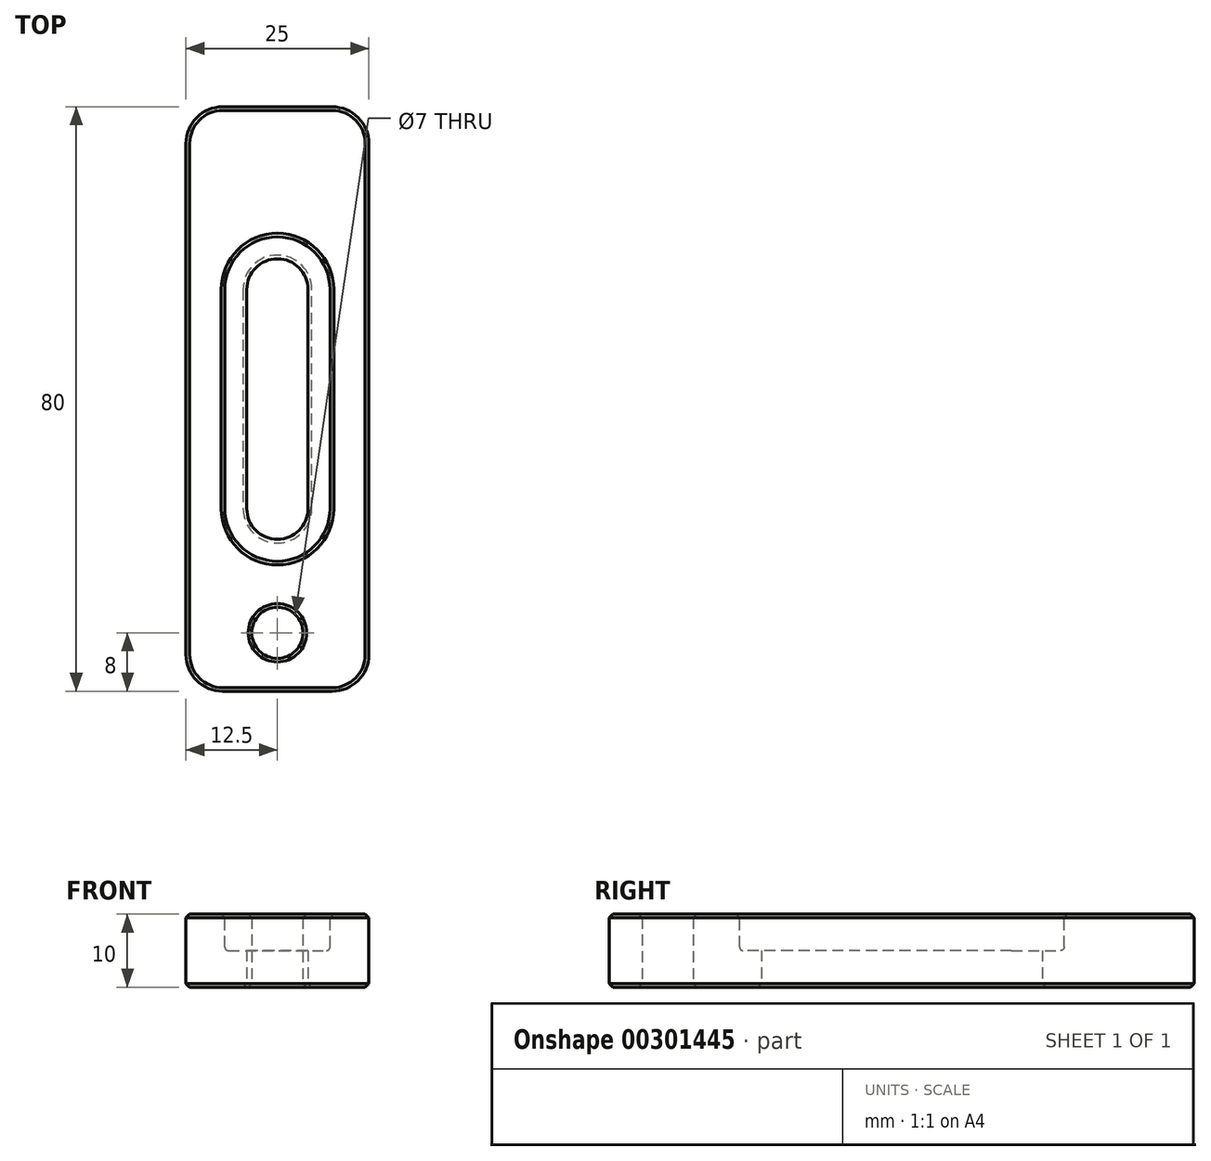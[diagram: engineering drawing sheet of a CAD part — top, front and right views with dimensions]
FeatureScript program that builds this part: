
annotation { "Feature Type Name" : "Feature", "Feature Type Description" : "" }
export const myFeature = defineFeature(function(context is Context, id is Id, definition is map)
    precondition{}
    {
        {
            var Q0;
            Q0=qCreatedBy(makeId("Top.planeOp"),FACE);
            var sketch = newSketch(context, id + "F0", { "sketchPlane" : qUnion([Q0])});
            skCircle(sketch, "E0", {"center": v(0, 15) * mm, "radius": 4.2 * mm});
            skLineSegment(sketch, "E1", {"start": v(0, 0) * mm, "end": v(25.4, 0) * mm, "construction": true});
            skCircle(sketch, "E2.MirrorC", {"center": v(0, -15) * mm, "radius": 4.2 * mm});
            skLineSegment(sketch, "E3", {"start": v(-4.2, 15) * mm, "end": v(-4.2, -15) * mm});
            skLineSegment(sketch, "E4", {"start": v(0, 0) * mm, "end": v(0, 38.64) * mm, "construction": true});
            skLineSegment(sketch, "E5.MirrorCS", {"start": v(4.2, 15) * mm, "end": v(4.2, -15) * mm});
            skLineSegment(sketch, "E6.bottom", {"start": v(-12.5, 40) * mm, "end": v(12.5, 40) * mm});
            skLineSegment(sketch, "E6.top", {"start": v(-12.5, -40) * mm, "end": v(12.5, -40) * mm});
            skLineSegment(sketch, "E6.left", {"start": v(-12.5, 40) * mm, "end": v(-12.5, -40) * mm});
            skLineSegment(sketch, "E6.right", {"start": v(12.5, 40) * mm, "end": v(12.5, -40) * mm});
            skCircle(sketch, "E7", {"center": v(0, -32) * mm, "radius": 3.5 * mm});
            skSolve(sketch);
        }
        {
            var Q0;
            Q0 = qSketchRegion(id + "F0", true);
            extrude(context, id + "F1", {"entities" : qUnion([Q0]), "depth" : 10 * mm});
        }
        {
            var Q0;
            Q0=makeQuery(id+"F1.opExtrude","CAP_FACE",FACE,{"disambiguationData":[OSD([sQuery(id+"F0.wireOp",EDGE,"E0"),sQuery(id+"F0.wireOp",EDGE,"E2.MirrorC"),sQuery(id+"F0.wireOp",EDGE,"E3"),sQuery(id+"F0.wireOp",EDGE,"E5.MirrorCS"),sQuery(id+"F0.wireOp",EDGE,"E6.bottom"),sQuery(id+"F0.wireOp",EDGE,"E6.top"),sQuery(id+"F0.wireOp",EDGE,"E6.left"),sQuery(id+"F0.wireOp",EDGE,"E6.right"),sQuery(id+"F0.wireOp",EDGE,"E7")])],"isStart":false});
            var sketch = newSketch(context, id + "F2", { "sketchPlane" : qUnion([Q0])});
            skArc(sketch, "E8.0", {"start": v(4.2, 15) * mm, "mid": v(0, 19.2) * mm, "end": v(-4.2, 15) * mm});
            skLineSegment(sketch, "E9.0", {"start": v(-4.2, 15) * mm, "end": v(-4.2, -15) * mm});
            skLineSegment(sketch, "E10.0", {"start": v(4.2, 15) * mm, "end": v(4.2, -15) * mm});
            skArc(sketch, "E11.0", {"start": v(4.2, -15) * mm, "mid": v(0, -19.2) * mm, "end": v(-4.2, -15) * mm});
            skLineSegment(sketch, "E12.0", {"start": v(7.2, 15) * mm, "end": v(7.2, -15) * mm});
            skArc(sketch, "E12.1", {"start": v(7.2, 15) * mm, "mid": v(0, 22.2) * mm, "end": v(-7.2, 15) * mm});
            skLineSegment(sketch, "E12.2", {"start": v(-7.2, 15) * mm, "end": v(-7.2, -15) * mm});
            skArc(sketch, "E12.3", {"start": v(7.2, -15) * mm, "mid": v(0, -22.2) * mm, "end": v(-7.2, -15) * mm});
            skSolve(sketch);
        }
        {
            var Q0;
            Q0=makeQuery(id+"F2.imprint","IMPRINT",FACE,{"disambiguationData":[TD([[makeQuery(id+"F2.imprint","IMPRINT",EDGE,{"derivedFrom":sQuery(id+"F2.wireOp",EDGE,"E8.0")}),-1.0]])]});
            extrude(context, id + "F3", {"entities" : qUnion([Q0]), "operationType" : NewBodyOperationType.REMOVE, "oppositeDirection" : true, "depth" : 5 * mm});
        }
        {
            var Q0;
            Q0=makeQuery(id+"F1.opExtrude","SWEPT_EDGE",EDGE,{"disambiguationData":[OSD([sQuery(id+"F0.wireOp",EDGE,"E6.bottom"),sQuery(id+"F0.wireOp",EDGE,"E6.right")])]});
            var Q1;
            Q1=makeQuery(id+"F1.opExtrude","SWEPT_EDGE",EDGE,{"disambiguationData":[OSD([sQuery(id+"F0.wireOp",EDGE,"E6.top"),sQuery(id+"F0.wireOp",EDGE,"E6.left")])]});
            var Q2;
            Q2=makeQuery(id+"F1.opExtrude","SWEPT_EDGE",EDGE,{"disambiguationData":[OSD([sQuery(id+"F0.wireOp",EDGE,"E6.top"),sQuery(id+"F0.wireOp",EDGE,"E6.right")])]});
            var Q3;
            Q3=makeQuery(id+"F1.opExtrude","SWEPT_EDGE",EDGE,{"disambiguationData":[OSD([sQuery(id+"F0.wireOp",EDGE,"E6.bottom"),sQuery(id+"F0.wireOp",EDGE,"E6.left")])]});
            fillet(context, id + "F4", {"entities" : qUnion([Q0, Q1, Q2, Q3]), "radius" : 5 * mm, "tangentPropagation" : true, "allowEdgeOverflow" : false});
        }
        {
            var Q0;
            Q0=makeQuery(id+"F1.opExtrude","CAP_FACE",FACE,{"disambiguationData":[OSD([sQuery(id+"F0.wireOp",EDGE,"E0"),sQuery(id+"F0.wireOp",EDGE,"E2.MirrorC"),sQuery(id+"F0.wireOp",EDGE,"E3"),sQuery(id+"F0.wireOp",EDGE,"E5.MirrorCS"),sQuery(id+"F0.wireOp",EDGE,"E6.bottom"),sQuery(id+"F0.wireOp",EDGE,"E6.top"),sQuery(id+"F0.wireOp",EDGE,"E6.left"),sQuery(id+"F0.wireOp",EDGE,"E6.right"),sQuery(id+"F0.wireOp",EDGE,"E7")])],"isStart":false});
            var Q1;
            Q1=makeQuery(id+"F1.opExtrude","CAP_FACE",FACE,{"disambiguationData":[OSD([sQuery(id+"F0.wireOp",EDGE,"E0"),sQuery(id+"F0.wireOp",EDGE,"E2.MirrorC"),sQuery(id+"F0.wireOp",EDGE,"E3"),sQuery(id+"F0.wireOp",EDGE,"E5.MirrorCS"),sQuery(id+"F0.wireOp",EDGE,"E6.bottom"),sQuery(id+"F0.wireOp",EDGE,"E6.top"),sQuery(id+"F0.wireOp",EDGE,"E6.left"),sQuery(id+"F0.wireOp",EDGE,"E6.right"),sQuery(id+"F0.wireOp",EDGE,"E7")])],"isStart":true});
            chamfer(context, id + "F5", {"entities" : qUnion([Q0, Q1]), "width" : .5 * mm, "tangentPropagation" : true});
        }
        {
            var Q0;
            Q0=makeQuery(id+"F3.boolean.opBoolean","COPY",EDGE,{"derivedFrom":makeQuery(id+"F3.opExtrude","CAP_EDGE",EDGE,{"disambiguationData":[OSD([sQuery(id+"F2.wireOp",EDGE,"E12.1")])],"isStart":false})});
            fillet(context, id + "F6", {"entities" : qUnion([Q0]), "radius" : .5 * mm, "tangentPropagation" : true, "allowEdgeOverflow" : false});
        }
    });
